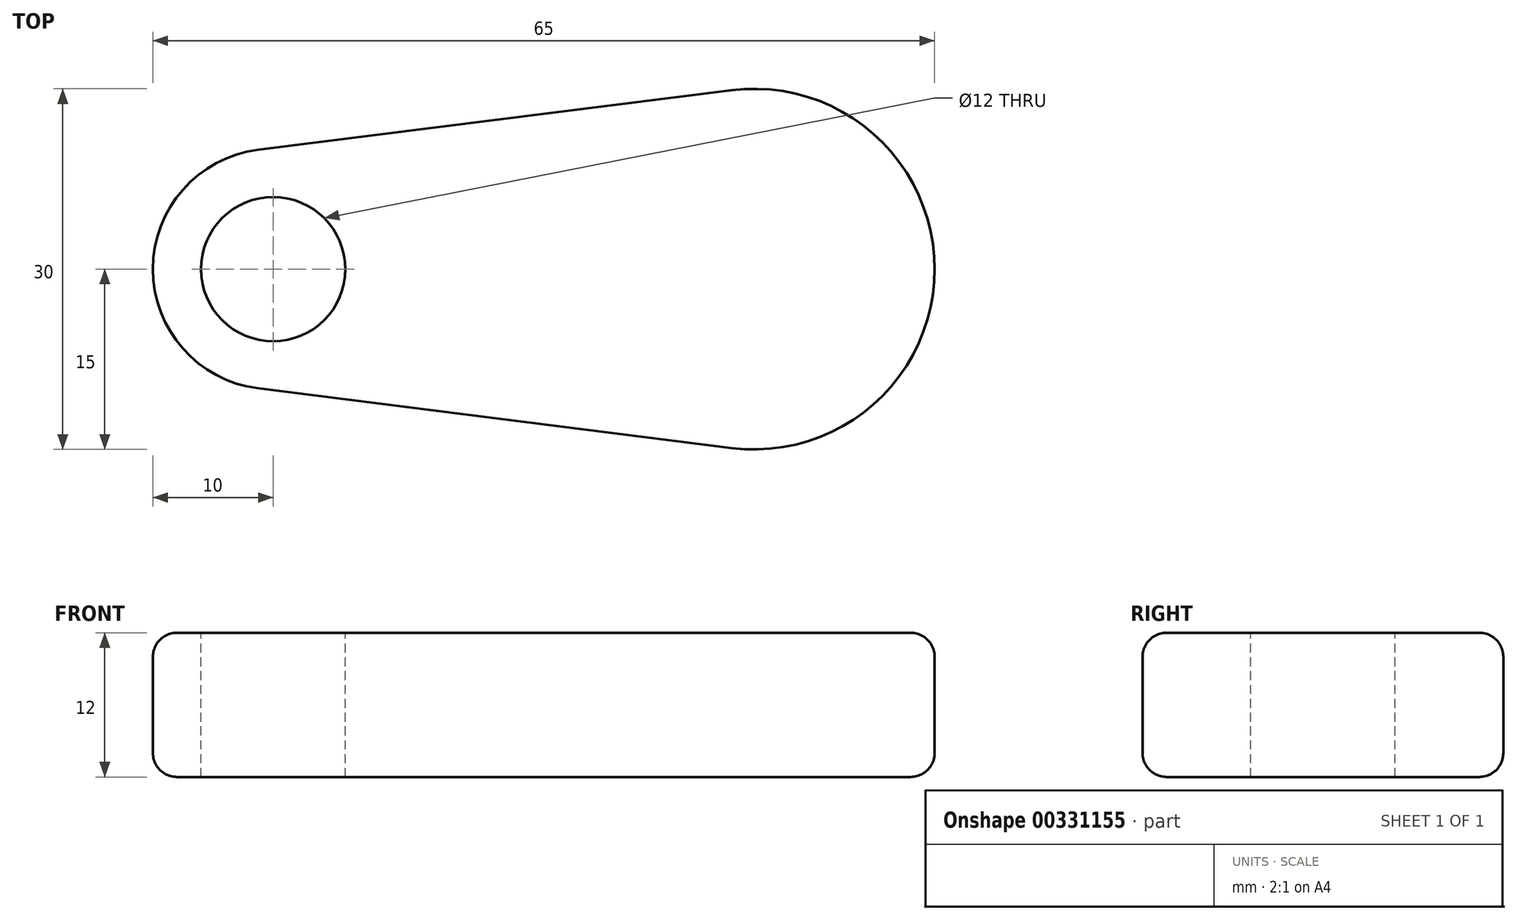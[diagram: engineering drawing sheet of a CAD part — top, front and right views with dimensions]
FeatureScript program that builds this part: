
annotation { "Feature Type Name" : "Feature", "Feature Type Description" : "" }
export const myFeature = defineFeature(function(context is Context, id is Id, definition is map)
    precondition{}
    {
        {
            var Q0;
            Q0=qCreatedBy(makeId("Top.planeOp"),FACE);
            var sketch = newSketch(context, id + "F0", { "sketchPlane" : qUnion([Q0])});
            skArc(sketch, "E0", {"start": v(-1.25, 9.92) * mm, "mid": v(-10, 0) * mm, "end": v(-1.25, -9.92) * mm});
            skArc(sketch, "E1", {"start": v(38.12, -14.88) * mm, "mid": v(55, 0) * mm, "end": v(38.13, 14.88) * mm});
            skLineSegment(sketch, "E2", {"start": v(-1.25, 9.92) * mm, "end": v(38.13, 14.88) * mm});
            skLineSegment(sketch, "E3", {"start": v(-1.25, -9.92) * mm, "end": v(38.12, -14.88) * mm});
            skSolve(sketch);
        }
        {
            var Q0;
            Q0=makeQuery(id+"F0.imprint","IMPRINT",FACE,{"disambiguationData":[TD([[makeQuery(id+"F0.imprint","IMPRINT",EDGE,{"derivedFrom":sQuery(id+"F0.wireOp",EDGE,"E0")}),1.0]])]});
            extrude(context, id + "F1", {"entities" : qUnion([Q0]), "depth" : 12 * mm});
        }
        {
            var Q0;
            Q0=makeQuery(id+"F1.opExtrude","CAP_FACE",FACE,{"disambiguationData":[OSD([sQuery(id+"F0.wireOp",EDGE,"E0"),sQuery(id+"F0.wireOp",EDGE,"E1"),sQuery(id+"F0.wireOp",EDGE,"E2"),sQuery(id+"F0.wireOp",EDGE,"E3")])],"isStart":false});
            var sketch = newSketch(context, id + "F2", { "sketchPlane" : qUnion([Q0])});
            skCircle(sketch, "E4", {"center": v(0, 0) * mm, "radius": 6 * mm});
            skSolve(sketch);
        }
        {
            var Q0;
            Q0=makeQuery(id+"F2.imprint","IMPRINT",FACE,{"disambiguationData":[TD([[makeQuery(id+"F2.imprint","IMPRINT",EDGE,{"derivedFrom":sQuery(id+"F2.wireOp",EDGE,"E4")}),1.0]])]});
            extrude(context, id + "F3", {"entities" : qUnion([Q0]), "operationType" : NewBodyOperationType.REMOVE, "endBound" : BoundingType.UP_TO_NEXT, "oppositeDirection" : true, "depth" : 25 * mm});
        }
        {
            var Q0;
            Q0=makeQuery(id+"F1.opExtrude","CAP_EDGE",EDGE,{"disambiguationData":[OSD([sQuery(id+"F0.wireOp",EDGE,"E2")])],"isStart":false});
            var Q1;
            Q1=makeQuery(id+"F1.opExtrude","CAP_EDGE",EDGE,{"disambiguationData":[OSD([sQuery(id+"F0.wireOp",EDGE,"E2")])],"isStart":true});
            fillet(context, id + "F4", {"entities" : qUnion([Q0, Q1]), "radius" : 2 * mm, "tangentPropagation" : true, "allowEdgeOverflow" : false});
        }
    });
